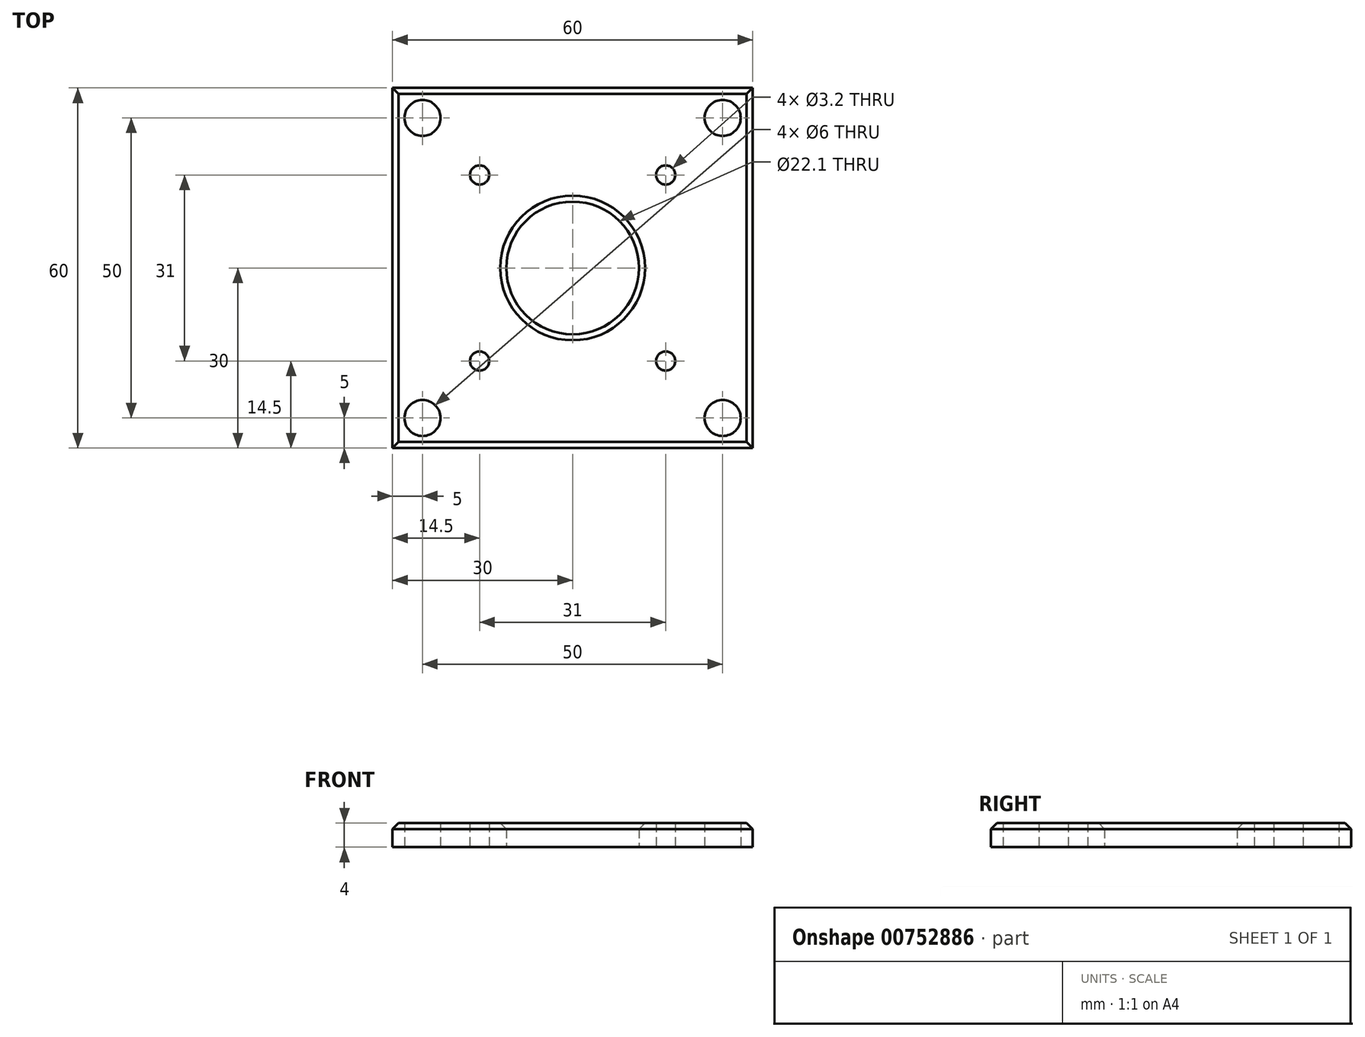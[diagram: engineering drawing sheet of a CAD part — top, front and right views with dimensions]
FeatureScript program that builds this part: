
annotation { "Feature Type Name" : "Feature", "Feature Type Description" : "" }
export const myFeature = defineFeature(function(context is Context, id is Id, definition is map)
    precondition{}
    {
        {
            var Q0;
            Q0=qCreatedBy(makeId("Top.planeOp"),FACE);
            var sketch = newSketch(context, id + "F0", { "sketchPlane" : qUnion([Q0])});
            skLineSegment(sketch, "E0.bottom", {"start": v(-30, 30) * mm, "end": v(30, 30) * mm});
            skLineSegment(sketch, "E0.top", {"start": v(-30, -30) * mm, "end": v(30, -30) * mm});
            skLineSegment(sketch, "E0.left", {"start": v(-30, 30) * mm, "end": v(-30, -30) * mm});
            skLineSegment(sketch, "E0.right", {"start": v(30, 30) * mm, "end": v(30, -30) * mm});
            skPoint(sketch, "E0.middle", {"position": v(0, 0) * mm});
            skLineSegment(sketch, "E1.bottom", {"start": v(-15.5, 15.5) * mm, "end": v(15.5, 15.5) * mm, "construction": true});
            skLineSegment(sketch, "E1.top", {"start": v(-15.5, -15.5) * mm, "end": v(15.5, -15.5) * mm, "construction": true});
            skLineSegment(sketch, "E1.left", {"start": v(-15.5, 15.5) * mm, "end": v(-15.5, -15.5) * mm, "construction": true});
            skLineSegment(sketch, "E1.right", {"start": v(15.5, 15.5) * mm, "end": v(15.5, -15.5) * mm, "construction": true});
            skLineSegment(sketch, "E2.bottom", {"start": v(-25, 25) * mm, "end": v(25, 25) * mm, "construction": true});
            skLineSegment(sketch, "E2.top", {"start": v(-25, -25) * mm, "end": v(25, -25) * mm, "construction": true});
            skLineSegment(sketch, "E2.left", {"start": v(-25, 25) * mm, "end": v(-25, -25) * mm, "construction": true});
            skLineSegment(sketch, "E2.right", {"start": v(25, 25) * mm, "end": v(25, -25) * mm, "construction": true});
            skCircle(sketch, "E3", {"center": v(0, 0) * mm, "radius": 11.05 * mm});
            skSolve(sketch);
        }
        {
            var Q0;
            Q0=makeQuery(id+"F0.imprint","IMPRINT",FACE,{"disambiguationData":[TD([[makeQuery(id+"F0.imprint","IMPRINT",EDGE,{"derivedFrom":sQuery(id+"F0.wireOp",EDGE,"E0.bottom")}),-1.0]])]});
            extrude(context, id + "F1", {"entities" : qUnion([Q0]), "depth" : 4 * mm, "offsetDistance" : 25 * mm});
        }
        {
            var Q0;
            Q0=sQuery(id+"F0.wireOp",VERTEX,"E1.top.end");
            var Q1;
            Q1=sQuery(id+"F0.wireOp",VERTEX,"E1.bottom.end");
            var Q2;
            Q2=sQuery(id+"F0.wireOp",VERTEX,"E1.bottom.start");
            var Q3;
            Q3=sQuery(id+"F0.wireOp",VERTEX,"E1.top.start");
            var Q4;
            Q4=makeQuery(id+"F1.opExtrude","SWEPT_BODY",BODY,{"disambiguationData":[OSD([sQuery(id+"F0.wireOp",EDGE,"E0.bottom"),sQuery(id+"F0.wireOp",EDGE,"E0.top"),sQuery(id+"F0.wireOp",EDGE,"E0.left"),sQuery(id+"F0.wireOp",EDGE,"E0.right"),sQuery(id+"F0.wireOp",EDGE,"E3")])]});
            hole(context, id + "F2", {"style" : HoleStyle.SIMPLE, "endStyle" : HoleEndStyle.THROUGH, "oppositeDirection" : true, "standardTappedOrClearance" : lookupTablePath({ "fit" : "Close", "standard" : "ISO", "size" : "M3", "type" : "Clearance" }), "standardBlindInLast" : lookupTablePath({ "fit" : "Close", "standard" : "ISO", "engagement" : "75%", "pitch" : "0.5 mm", "size" : "M3", "type" : "Clearance & tapped" }), "holeDiameter" : 3.2 * mm, "majorDiameter" : 5 * mm, "isTappedThrough" : true, "tappedDepth" : 5 * mm, "tapClearance" : 3, "locations" : qUnion([Q0, Q1, Q2, Q3]), "scope" : qUnion([Q4])});
        }
        {
            var Q0;
            Q0=sQuery(id+"F0.wireOp",VERTEX,"E2.bottom.start");
            var Q1;
            Q1=sQuery(id+"F0.wireOp",VERTEX,"E2.bottom.end");
            var Q2;
            Q2=sQuery(id+"F0.wireOp",VERTEX,"E2.top.end");
            var Q3;
            Q3=sQuery(id+"F0.wireOp",VERTEX,"E2.top.start");
            var Q4;
            Q4=makeQuery(id+"F1.opExtrude","SWEPT_BODY",BODY,{"disambiguationData":[OSD([sQuery(id+"F0.wireOp",EDGE,"E0.bottom"),sQuery(id+"F0.wireOp",EDGE,"E0.top"),sQuery(id+"F0.wireOp",EDGE,"E0.left"),sQuery(id+"F0.wireOp",EDGE,"E0.right"),sQuery(id+"F0.wireOp",EDGE,"E3")])]});
            hole(context, id + "F3", {"style" : HoleStyle.SIMPLE, "endStyle" : HoleEndStyle.THROUGH, "oppositeDirection" : true, "standardTappedOrClearance" : lookupTablePath({ "standard" : "ISO", "size" : "6", "type" : "Drilled" }), "standardBlindInLast" : lookupTablePath({ "standard" : "ISO", "size" : "6", "type" : "Drilled" }), "holeDiameter" : 6 * mm, "majorDiameter" : 5 * mm, "isTappedThrough" : true, "tappedDepth" : 5 * mm, "tapClearance" : 3, "locations" : qUnion([Q0, Q1, Q2, Q3]), "scope" : qUnion([Q4])});
        }
        {
            var Q0;
            Q0=makeQuery(id+"F1.opExtrude","CAP_EDGE",EDGE,{"disambiguationData":[OSD([sQuery(id+"F0.wireOp",EDGE,"E3")])],"isStart":false});
            var Q1;
            Q1=makeQuery(id+"F1.opExtrude","CAP_EDGE",EDGE,{"disambiguationData":[OSD([sQuery(id+"F0.wireOp",EDGE,"E0.top")])],"isStart":false});
            var Q2;
            Q2=makeQuery(id+"F1.opExtrude","CAP_EDGE",EDGE,{"disambiguationData":[OSD([sQuery(id+"F0.wireOp",EDGE,"E0.left")])],"isStart":false});
            var Q3;
            Q3=makeQuery(id+"F1.opExtrude","CAP_EDGE",EDGE,{"disambiguationData":[OSD([sQuery(id+"F0.wireOp",EDGE,"E0.bottom")])],"isStart":false});
            var Q4;
            Q4=makeQuery(id+"F1.opExtrude","CAP_EDGE",EDGE,{"disambiguationData":[OSD([sQuery(id+"F0.wireOp",EDGE,"E0.right")])],"isStart":false});
            chamfer(context, id + "F4", {"entities" : qUnion([Q0, Q1, Q2, Q3, Q4]), "width" : 1 * mm, "tangentPropagation" : true});
        }
    });
